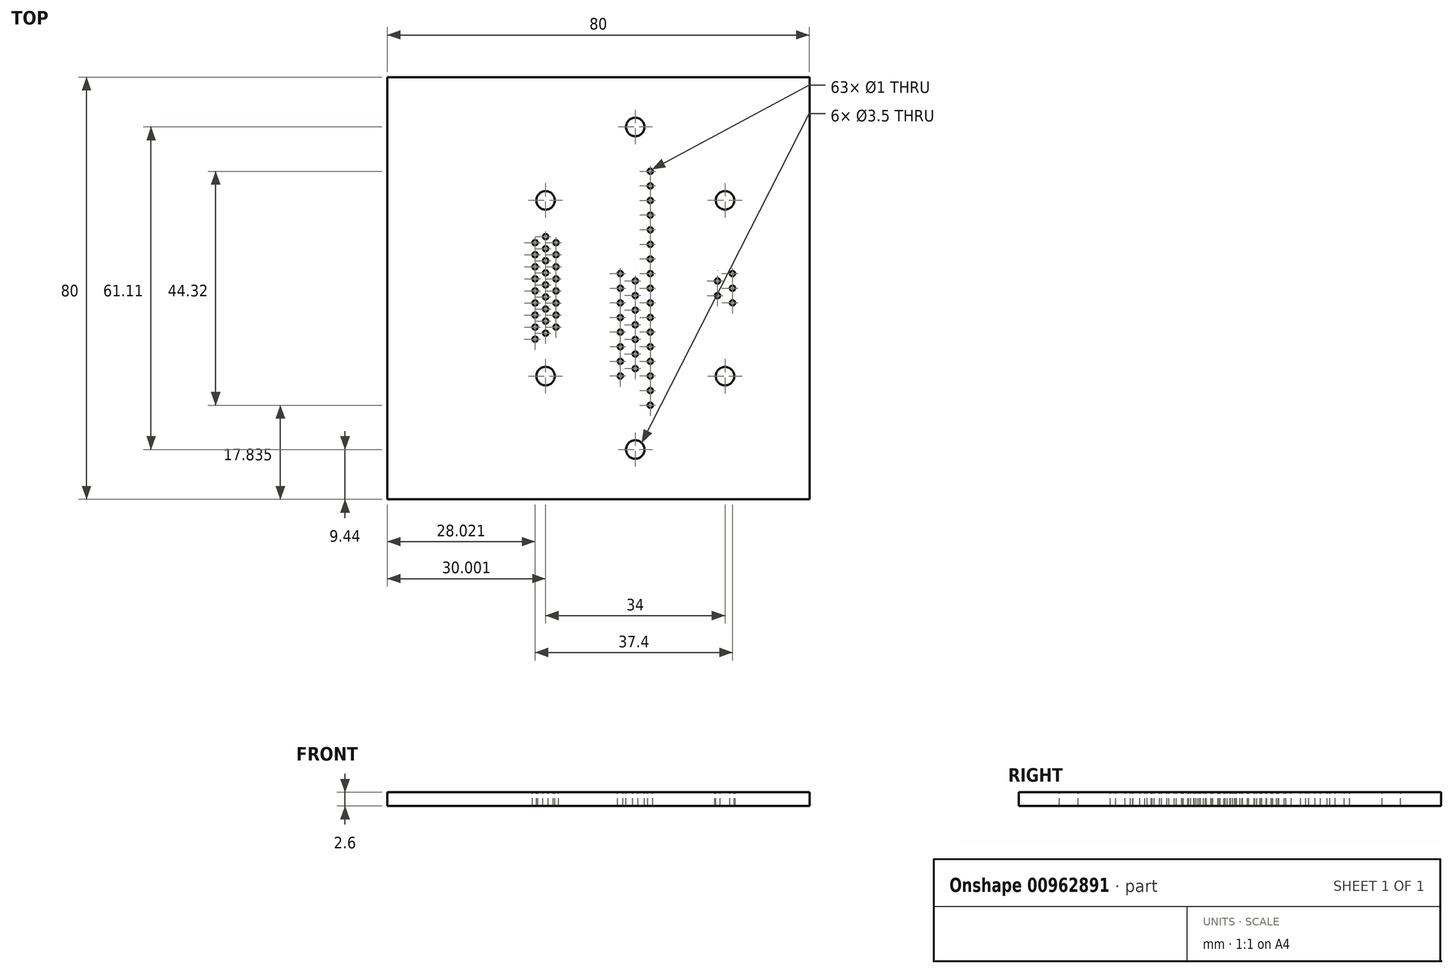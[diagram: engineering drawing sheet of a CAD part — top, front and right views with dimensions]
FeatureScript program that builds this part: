
annotation { "Feature Type Name" : "Feature", "Feature Type Description" : "" }
export const myFeature = defineFeature(function(context is Context, id is Id, definition is map)
    precondition{}
    {
        {
            var Q0;
            Q0=qCreatedBy(makeId("Top.planeOp"),FACE);
            var sketch = newSketch(context, id + "F0", { "sketchPlane" : qUnion([Q0])});
            skLineSegment(sketch, "E0.bottom", {"start": v(-43.16, 58.34) * mm, "end": v(36.84, 58.34) * mm});
            skLineSegment(sketch, "E0.top", {"start": v(-43.16, -21.66) * mm, "end": v(36.84, -21.66) * mm});
            skLineSegment(sketch, "E0.left", {"start": v(-43.16, 58.34) * mm, "end": v(-43.16, -21.66) * mm});
            skLineSegment(sketch, "E0.right", {"start": v(36.84, 58.34) * mm, "end": v(36.84, -21.66) * mm});
            skSolve(sketch);
        }
        {
            var Q0;
            Q0=makeQuery(id+"F0.imprint","IMPRINT",FACE,{"disambiguationData":[TD([[makeQuery(id+"F0.imprint","IMPRINT",EDGE,{"derivedFrom":sQuery(id+"F0.wireOp",EDGE,"E0.bottom")}),-1.0]])]});
            extrude(context, id + "F1", {"entities" : qUnion([Q0]), "depth" : 2.6 * mm, "offsetDistance" : 25 * mm});
        }
        {
            var Q0;
            {var subQ0=sQuery(id+"F0.wireOp",EDGE,"E0.left");var subQ1=sQuery(id+"F0.wireOp",EDGE,"E0.bottom");var subQ2=sQuery(id+"F0.wireOp",EDGE,"E0.right");var subQ3=sQuery(id+"F0.wireOp",EDGE,"E0.top");Q0=makeQuery(id+"F2.boolean.opBoolean","SPLIT",FACE,{"disambiguationData":[TD([makeQuery(id+"F1.opExtrude","SWEPT_FACE",FACE,{"disambiguationData":[OSD([subQ1])]})])],"derivedFrom":makeQuery(id+"F1.opExtrude","CAP_FACE",FACE,{"disambiguationData":[OSD([subQ1,subQ3,subQ0,subQ2])],"isStart":false})});}
            var sketch = newSketch(context, id + "F3", { "sketchPlane" : qUnion([Q0])});
            skCircle(sketch, "E1", {"center": v(-13.16, 1.69) * mm, "radius": 1.75 * mm});
            skCircle(sketch, "E2", {"center": v(-13.16, 34.99) * mm, "radius": 1.75 * mm});
            skCircle(sketch, "E3", {"center": v(-15.14, 8.68) * mm, "radius": 0.5 * mm});
            skCircle(sketch, "E4", {"center": v(-15.14, 10.97) * mm, "radius": 0.5 * mm});
            skCircle(sketch, "E5", {"center": v(-15.14, 13.26) * mm, "radius": 0.5 * mm});
            skCircle(sketch, "E6", {"center": v(-15.14, 15.54) * mm, "radius": 0.5 * mm});
            skCircle(sketch, "E7", {"center": v(-15.14, 17.83) * mm, "radius": 0.5 * mm});
            skCircle(sketch, "E8", {"center": v(-15.14, 20.11) * mm, "radius": 0.5 * mm});
            skCircle(sketch, "E9", {"center": v(-15.14, 22.4) * mm, "radius": 0.5 * mm});
            skCircle(sketch, "E10", {"center": v(-15.14, 24.69) * mm, "radius": 0.5 * mm});
            skCircle(sketch, "E11", {"center": v(-15.14, 26.97) * mm, "radius": 0.5 * mm});
            skCircle(sketch, "E12", {"center": v(-13.16, 9.83) * mm, "radius": 0.5 * mm});
            skCircle(sketch, "E13", {"center": v(-13.16, 12.11) * mm, "radius": 0.5 * mm});
            skCircle(sketch, "E14", {"center": v(-13.16, 14.4) * mm, "radius": 0.5 * mm});
            skCircle(sketch, "E15", {"center": v(-13.16, 16.68) * mm, "radius": 0.5 * mm});
            skCircle(sketch, "E16", {"center": v(-13.16, 18.97) * mm, "radius": 0.5 * mm});
            skCircle(sketch, "E17", {"center": v(-13.16, 21.26) * mm, "radius": 0.5 * mm});
            skCircle(sketch, "E18", {"center": v(-13.16, 23.54) * mm, "radius": 0.5 * mm});
            skCircle(sketch, "E19", {"center": v(-13.16, 25.83) * mm, "radius": 0.5 * mm});
            skCircle(sketch, "E20", {"center": v(-13.16, 28.11) * mm, "radius": 0.5 * mm});
            skCircle(sketch, "E21", {"center": v(-11.18, 10.97) * mm, "radius": 0.5 * mm});
            skCircle(sketch, "E22", {"center": v(-11.18, 13.26) * mm, "radius": 0.5 * mm});
            skCircle(sketch, "E23", {"center": v(-11.18, 15.54) * mm, "radius": 0.5 * mm});
            skCircle(sketch, "E24", {"center": v(-11.18, 17.83) * mm, "radius": 0.5 * mm});
            skCircle(sketch, "E25", {"center": v(-11.18, 20.11) * mm, "radius": 0.5 * mm});
            skCircle(sketch, "E26", {"center": v(-11.18, 22.4) * mm, "radius": 0.5 * mm});
            skCircle(sketch, "E27", {"center": v(-11.18, 24.69) * mm, "radius": 0.5 * mm});
            skCircle(sketch, "E28", {"center": v(-11.18, 26.97) * mm, "radius": 0.5 * mm});
            skCircle(sketch, "E29", {"center": v(3.84, -12.22) * mm, "radius": 1.75 * mm});
            skCircle(sketch, "E30", {"center": v(3.84, 48.9) * mm, "radius": 1.75 * mm});
            skCircle(sketch, "E31", {"center": v(6.68, -3.82) * mm, "radius": 0.5 * mm});
            skCircle(sketch, "E32", {"center": v(6.68, -1.05) * mm, "radius": 0.5 * mm});
            skCircle(sketch, "E33", {"center": v(6.68, 1.72) * mm, "radius": 0.5 * mm});
            skCircle(sketch, "E34", {"center": v(6.68, 4.49) * mm, "radius": 0.5 * mm});
            skCircle(sketch, "E35", {"center": v(6.68, 7.26) * mm, "radius": 0.5 * mm});
            skCircle(sketch, "E36", {"center": v(6.68, 10.03) * mm, "radius": 0.5 * mm});
            skCircle(sketch, "E37", {"center": v(6.68, 12.8) * mm, "radius": 0.5 * mm});
            skCircle(sketch, "E38", {"center": v(6.68, 15.57) * mm, "radius": 0.5 * mm});
            skCircle(sketch, "E39", {"center": v(6.68, 18.34) * mm, "radius": 0.5 * mm});
            skCircle(sketch, "E40", {"center": v(6.68, 21.1) * mm, "radius": 0.5 * mm});
            skCircle(sketch, "E41", {"center": v(6.68, 23.88) * mm, "radius": 0.5 * mm});
            skCircle(sketch, "E42", {"center": v(6.68, 26.65) * mm, "radius": 0.5 * mm});
            skCircle(sketch, "E43", {"center": v(6.68, 29.42) * mm, "radius": 0.5 * mm});
            skCircle(sketch, "E44", {"center": v(6.68, 32.19) * mm, "radius": 0.5 * mm});
            skCircle(sketch, "E45", {"center": v(6.68, 34.96) * mm, "radius": 0.5 * mm});
            skCircle(sketch, "E46", {"center": v(6.68, 37.73) * mm, "radius": 0.5 * mm});
            skCircle(sketch, "E47", {"center": v(6.68, 40.5) * mm, "radius": 0.5 * mm});
            skCircle(sketch, "E48", {"center": v(3.84, 3.1) * mm, "radius": 0.5 * mm});
            skCircle(sketch, "E49", {"center": v(3.84, 5.88) * mm, "radius": 0.5 * mm});
            skCircle(sketch, "E50", {"center": v(3.84, 8.65) * mm, "radius": 0.5 * mm});
            skCircle(sketch, "E51", {"center": v(3.84, 11.42) * mm, "radius": 0.5 * mm});
            skCircle(sketch, "E52", {"center": v(3.84, 14.19) * mm, "radius": 0.5 * mm});
            skCircle(sketch, "E53", {"center": v(3.84, 16.96) * mm, "radius": 0.5 * mm});
            skCircle(sketch, "E54", {"center": v(3.84, 19.73) * mm, "radius": 0.5 * mm});
            skCircle(sketch, "E55", {"center": v(1, 1.72) * mm, "radius": 0.5 * mm});
            skCircle(sketch, "E56", {"center": v(1, 4.49) * mm, "radius": 0.5 * mm});
            skCircle(sketch, "E57", {"center": v(1, 7.26) * mm, "radius": 0.5 * mm});
            skCircle(sketch, "E58", {"center": v(1, 10.03) * mm, "radius": 0.5 * mm});
            skCircle(sketch, "E59", {"center": v(1, 12.8) * mm, "radius": 0.5 * mm});
            skCircle(sketch, "E60", {"center": v(1, 15.57) * mm, "radius": 0.5 * mm});
            skCircle(sketch, "E61", {"center": v(1, 18.34) * mm, "radius": 0.5 * mm});
            skCircle(sketch, "E62", {"center": v(1, 21.1) * mm, "radius": 0.5 * mm});
            skCircle(sketch, "E63", {"center": v(20.84, 1.68) * mm, "radius": 1.75 * mm});
            skCircle(sketch, "E64", {"center": v(20.84, 35) * mm, "radius": 1.75 * mm});
            skCircle(sketch, "E65", {"center": v(22.26, 15.57) * mm, "radius": 0.5 * mm});
            skCircle(sketch, "E66", {"center": v(22.26, 18.34) * mm, "radius": 0.5 * mm});
            skCircle(sketch, "E67", {"center": v(22.26, 21.1) * mm, "radius": 0.5 * mm});
            skCircle(sketch, "E68", {"center": v(19.42, 16.94) * mm, "radius": 0.5 * mm});
            skCircle(sketch, "E69", {"center": v(19.42, 19.7) * mm, "radius": 0.5 * mm});
            skSolve(sketch);
        }
        {
            var Q0;
            Q0 = qSketchRegion(id + "F3", true);
            extrude(context, id + "F4", {"entities" : qUnion([Q0]), "operationType" : NewBodyOperationType.REMOVE, "endBound" : BoundingType.UP_TO_NEXT, "oppositeDirection" : true, "depth" : 25 * mm, "offsetDistance" : 25 * mm});
        }
    });
